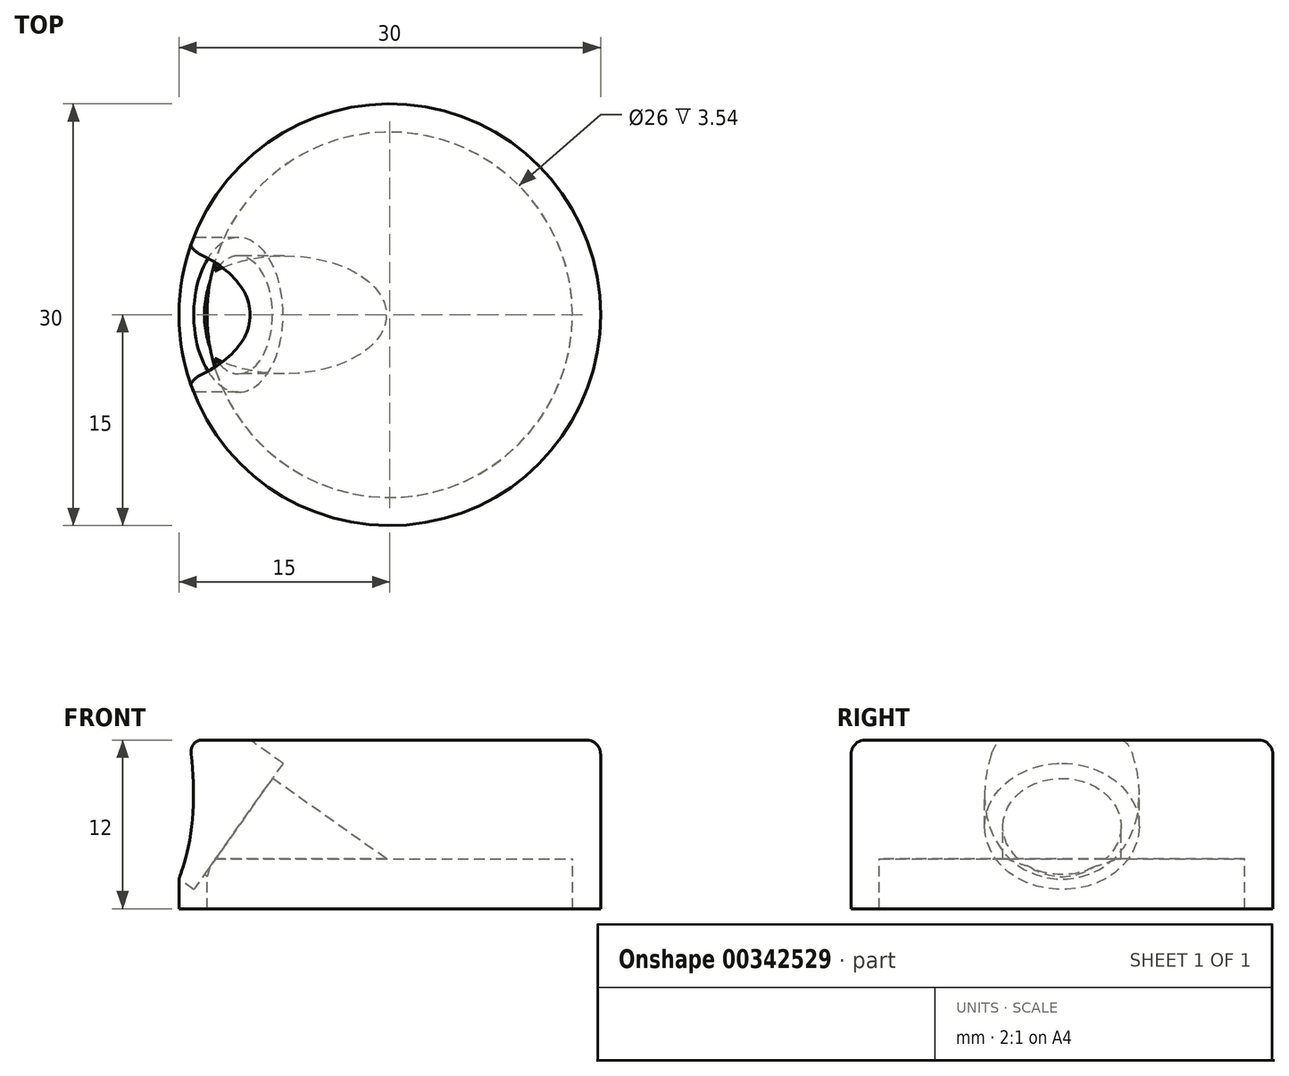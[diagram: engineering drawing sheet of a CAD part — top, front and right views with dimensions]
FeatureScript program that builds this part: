
annotation { "Feature Type Name" : "Feature", "Feature Type Description" : "" }
export const myFeature = defineFeature(function(context is Context, id is Id, definition is map)
    precondition{}
    {
        {
            var Q0;
            Q0=qCreatedBy(makeId("Top.planeOp"),FACE);
            var sketch = newSketch(context, id + "F0", { "sketchPlane" : qUnion([Q0])});
            skCircle(sketch, "E0", {"center": v(0, 0) * mm, "radius": 7.5 * mm, "construction": true});
            skPoint(sketch, "E1", {"position": v(0, 7.5) * mm});
            skPoint(sketch, "E2.1.0", {"position": v(-7.5, 0) * mm});
            skPoint(sketch, "E2.2.0", {"position": v(0, -7.5) * mm});
            skPoint(sketch, "E2.3.0", {"position": v(7.5, 0) * mm});
            skSolve(sketch);
        }
        {
            var Q0;
            Q0=qCreatedBy(makeId("Front.planeOp"),FACE);
            var sketch = newSketch(context, id + "F1", { "sketchPlane" : qUnion([Q0])});
            skLineSegment(sketch, "E3", {"start": v(0, 22.12) * mm, "end": v(0, -30.6) * mm, "construction": true});
            skSolve(sketch);
        }
        {
            var Q0;
            Q0=qCreatedBy(makeId("Top.planeOp"),FACE);
            cPlane(context, id + "F2", {"entities" : qUnion([Q0]), "cplaneType" : CPlaneType.OFFSET, "offset" : 3.54 * mm, "oppositeDirection" : true, "width" : 150 * mm, "height" : 150 * mm});
        }
        {
            var Q0;
            Q0=qCreatedBy(makeId("Front.planeOp"),FACE);
            var sketch = newSketch(context, id + "F3", { "sketchPlane" : qUnion([Q0])});
            skLineSegment(sketch, "E4", {"start": v(0, 8.46) * mm, "end": v(-15, 8.46) * mm});
            skLineSegment(sketch, "E5", {"start": v(-15, 8.46) * mm, "end": v(-15, -3.54) * mm});
            skLineSegment(sketch, "E6", {"start": v(-15, -3.54) * mm, "end": v(-13, -3.54) * mm});
            skLineSegment(sketch, "E7", {"start": v(-13, -3.54) * mm, "end": v(-13, 0) * mm});
            skLineSegment(sketch, "E8", {"start": v(-13, 0) * mm, "end": v(0, 0) * mm});
            skLineSegment(sketch, "E9", {"start": v(0, 8.46) * mm, "end": v(0, 0) * mm});
            skSolve(sketch);
        }
        {
            var Q0;
            Q0 = qSketchRegion(id + "F3", true);
            var Q1;
            Q1=sQuery(id+"F1.wireOp",EDGE,"E3");
            revolve(context, id + "F4", {"entities" : qUnion([Q0]), "axis" : qUnion([Q1]), "revolveType" : RevolveType.FULL});
        }
        {
            var Q0;
            Q0=qCreatedBy(makeId("Front.planeOp"),FACE);
            var sketch = newSketch(context, id + "F5", { "sketchPlane" : qUnion([Q0])});
            skLineSegment(sketch, "E10", {"start": v(-2.5, -1.18) * mm, "end": v(-2.5, -5.05) * mm, "construction": true});
            skLineSegment(sketch, "E11", {"start": v(-7.5, 1.83) * mm, "end": v(-7.5, -6.98) * mm, "construction": true});
            skLineSegment(sketch, "E12", {"start": v(0, -3.54) * mm, "end": v(-4.68, -3.54) * mm, "construction": true});
            skLineSegment(sketch, "E13", {"start": v(0, 0) * mm, "end": v(-9.21, 0) * mm, "construction": true});
            skPoint(sketch, "E14", {"position": v(-2.5, -3.54) * mm});
            skPoint(sketch, "E15", {"position": v(-7.5, 0) * mm});
            skLineSegment(sketch, "E16", {"start": v(-2.5, -3.54) * mm, "end": v(-17.3, 6.93) * mm, "construction": true});
            skLineSegment(sketch, "E17", {"start": v(-5.07, 3.43) * mm, "end": v(-8.34, 5.74) * mm});
            skLineSegment(sketch, "E18", {"start": v(-8.34, 5.74) * mm, "end": v(-7.59, 6.8) * mm});
            skLineSegment(sketch, "E19", {"start": v(-7.59, 6.8) * mm, "end": v(-14.12, 11.42) * mm});
            skLineSegment(sketch, "E20", {"start": v(-14.12, 11.42) * mm, "end": v(-17.3, 6.93) * mm});
            skLineSegment(sketch, "E21", {"start": v(-17.3, 6.93) * mm, "end": v(-7.5, 0) * mm});
            skLineSegment(sketch, "E22", {"start": v(-5.07, 3.43) * mm, "end": v(-0.18, -0.04) * mm});
            skLineSegment(sketch, "E23", {"start": v(-0.18, -0.04) * mm, "end": v(-2.6, -3.46) * mm});
            skLineSegment(sketch, "E24", {"start": v(-2.6, -3.46) * mm, "end": v(-7.5, 0) * mm});
            skSolve(sketch);
        }
        {
            var Q0;
            Q0 = qSketchRegion(id + "F5", true);
            var Q1;
            Q1=sQuery(id+"F5.wireOp",EDGE,"E16");
            revolve(context, id + "F6", {"operationType" : NewBodyOperationType.REMOVE, "entities" : qUnion([Q0]), "axis" : qUnion([Q1]), "revolveType" : RevolveType.FULL, "oppositeDirection" : true});
        }
        {
            var Q0;
            {var subQ0=sQuery(id+"F3.wireOp",EDGE,"E4");var subQ2=sQuery(id+"F3.wireOp",EDGE,"E5");var subQ4=sQuery(id+"F5.wireOp",EDGE,"E19");var subQ5=makeQuery(id+"F6.boolean.opBoolean","COPY",FACE,{"derivedFrom":makeQuery(id+"F6.opRevolve","SWEPT_FACE",FACE,{"disambiguationData":[OSD([subQ4])]})});Q0=makeQuery(id+"F8OCcc8s2irU87B_1.3.F6.boolean.opBoolean","SPLIT",EDGE,{"disambiguationData":[TD([subQ5])],"derivedFrom":makeQuery(id+"F8OCcc8s2irU87B_1.2.F6.boolean.opBoolean","SPLIT",EDGE,{"disambiguationData":[TD([subQ5])],"derivedFrom":makeQuery(id+"F8OCcc8s2irU87B_1.1.F6.boolean.opBoolean","SPLIT",EDGE,{"disambiguationData":[OD(0.0)],"derivedFrom":makeQuery(id+"F4.opRevolve","SWEPT_EDGE",EDGE,{"disambiguationData":[OSD([subQ0,subQ2])]})})})});}
            var Q1;
            {var subQ0=sQuery(id+"F3.wireOp",EDGE,"E4");var subQ2=sQuery(id+"F3.wireOp",EDGE,"E5");var subQ4=sQuery(id+"F5.wireOp",EDGE,"E19");var subQ5=makeQuery(id+"F8OCcc8s2irU87B_1.2.F6.opRevolve","SWEPT_FACE",FACE,{"disambiguationData":[OSD([subQ4])]});Q1=makeQuery(id+"F8OCcc8s2irU87B_1.3.F6.boolean.opBoolean","SPLIT",EDGE,{"disambiguationData":[TD([makeQuery(id+"F8OCcc8s2irU87B_1.2.F6.boolean.opBoolean","COPY",FACE,{"derivedFrom":subQ5})])],"derivedFrom":makeQuery(id+"F8OCcc8s2irU87B_1.2.F6.boolean.opBoolean","SPLIT",EDGE,{"disambiguationData":[TD([makeQuery(id+"F6.boolean.opBoolean","COPY",FACE,{"derivedFrom":makeQuery(id+"F6.opRevolve","SWEPT_FACE",FACE,{"disambiguationData":[OSD([subQ4])]})})])],"derivedFrom":makeQuery(id+"F8OCcc8s2irU87B_1.1.F6.boolean.opBoolean","SPLIT",EDGE,{"disambiguationData":[OD(0.0)],"derivedFrom":makeQuery(id+"F4.opRevolve","SWEPT_EDGE",EDGE,{"disambiguationData":[OSD([subQ0,subQ2])]})})})});}
            var Q2;
            {var subQ0=sQuery(id+"F3.wireOp",EDGE,"E4");var subQ1=sQuery(id+"F3.wireOp",EDGE,"E5");var subQ2=sQuery(id+"F5.wireOp",EDGE,"E19");Q2=makeQuery(id+"F8OCcc8s2irU87B_1.2.F6.boolean.opBoolean","SPLIT",EDGE,{"disambiguationData":[TD([makeQuery(id+"F8OCcc8s2irU87B_1.1.F6.boolean.opBoolean","COPY",FACE,{"derivedFrom":makeQuery(id+"F8OCcc8s2irU87B_1.1.F6.opRevolve","SWEPT_FACE",FACE,{"disambiguationData":[OSD([subQ2])]})})])],"derivedFrom":makeQuery(id+"F8OCcc8s2irU87B_1.1.F6.boolean.opBoolean","SPLIT",EDGE,{"disambiguationData":[OD(0.0)],"derivedFrom":makeQuery(id+"F4.opRevolve","SWEPT_EDGE",EDGE,{"disambiguationData":[OSD([subQ0,subQ1])]})})});}
            var Q3;
            Q3=makeQuery(id+"F8OCcc8s2irU87B_1.1.F6.boolean.opBoolean","SPLIT",EDGE,{"disambiguationData":[OD(1.0)],"derivedFrom":makeQuery(id+"F4.opRevolve","SWEPT_EDGE",EDGE,{"disambiguationData":[OSD([sQuery(id+"F3.wireOp",EDGE,"E4"),sQuery(id+"F3.wireOp",EDGE,"E5")])]})});
            fillet(context, id + "F7", {"entities" : qUnion([Q0, Q1, Q2, Q3]), "radius" : 1 * mm, "tangentPropagation" : true, "allowEdgeOverflow" : false});
        }
    });
